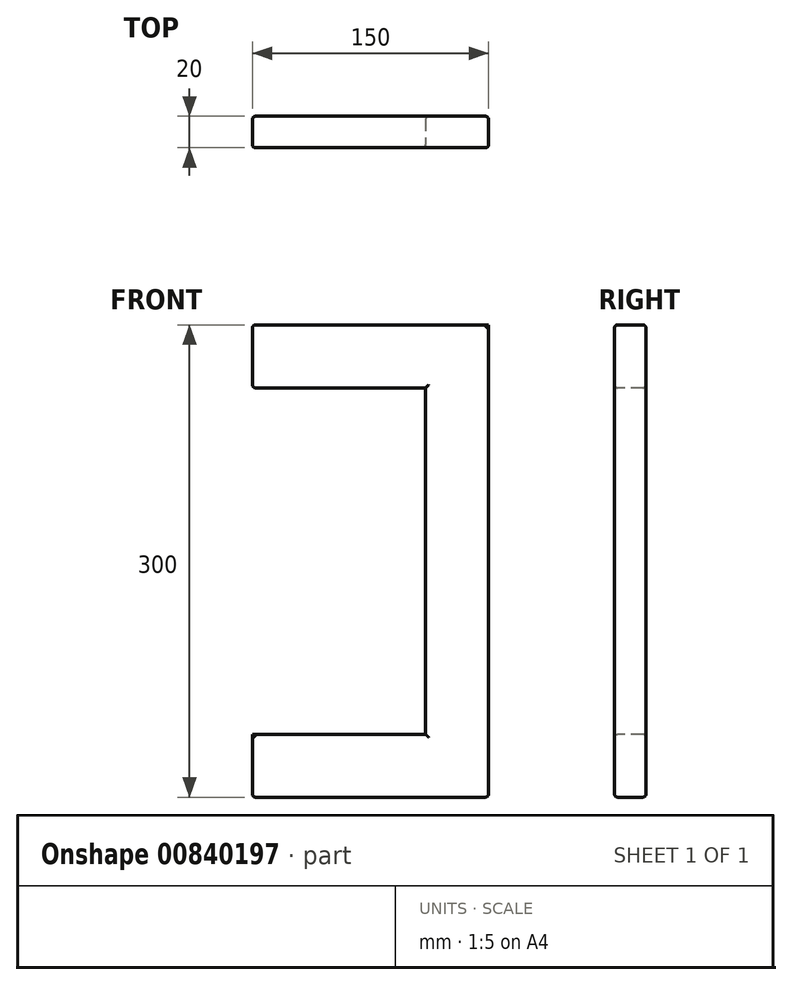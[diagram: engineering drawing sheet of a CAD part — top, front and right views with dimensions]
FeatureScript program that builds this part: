
annotation { "Feature Type Name" : "Feature", "Feature Type Description" : "" }
export const myFeature = defineFeature(function(context is Context, id is Id, definition is map)
    precondition{}
    {
        {
            var Q0;
            Q0=qCreatedBy(makeId("Top.planeOp"),FACE);
            var sketch = newSketch(context, id + "F0", { "sketchPlane" : qUnion([Q0])});
            skLineSegment(sketch, "E0.bottom", {"start": v(-48.59, 39.95) * mm, "end": v(-8.59, 39.95) * mm});
            skLineSegment(sketch, "E0.top", {"start": v(-48.59, 19.95) * mm, "end": v(-8.59, 19.95) * mm});
            skLineSegment(sketch, "E0.left", {"start": v(-48.59, 39.95) * mm, "end": v(-48.59, 19.95) * mm});
            skLineSegment(sketch, "E0.right", {"start": v(-8.59, 39.95) * mm, "end": v(-8.59, 19.95) * mm});
            skSolve(sketch);
        }
        {
            var Q0;
            Q0=makeQuery(id+"F0.imprint","IMPRINT",FACE,{"disambiguationData":[TD([[makeQuery(id+"F0.imprint","IMPRINT",EDGE,{"derivedFrom":sQuery(id+"F0.wireOp",EDGE,"E0.bottom")}),-1.0]])]});
            extrude(context, id + "F1", {"entities" : qUnion([Q0]), "depth" : 300 * mm, "offsetDistance" : 25 * mm});
        }
        {
            var Q0;
            Q0=makeQuery(id+"F1.opExtrude","SWEPT_FACE",FACE,{"disambiguationData":[OSD([sQuery(id+"F0.wireOp",EDGE,"E0.bottom")])]});
            var sketch = newSketch(context, id + "F2", { "sketchPlane" : qUnion([Q0])});
            skLineSegment(sketch, "E1", {"start": v(8.59, 300) * mm, "end": v(158.59, 300) * mm});
            skLineSegment(sketch, "E2", {"start": v(158.59, 300) * mm, "end": v(158.59, 260) * mm});
            skLineSegment(sketch, "E3", {"start": v(158.59, 260) * mm, "end": v(8.59, 260) * mm});
            skLineSegment(sketch, "E4", {"start": v(8.59, 260) * mm, "end": v(8.59, 300) * mm});
            skLineSegment(sketch, "E5", {"start": v(8.59, 0) * mm, "end": v(158.59, 0) * mm});
            skLineSegment(sketch, "E6", {"start": v(158.59, 0) * mm, "end": v(158.59, 40) * mm});
            skLineSegment(sketch, "E7", {"start": v(158.59, 40) * mm, "end": v(8.59, 40) * mm});
            skLineSegment(sketch, "E8", {"start": v(8.59, 40) * mm, "end": v(8.59, 0) * mm});
            skSolve(sketch);
        }
        {
            var Q0;
            {var subQ3=sQuery(id+"F2.wireOp",EDGE,"E2");Q0=makeQuery(id+"F2.imprint","IMPRINT",FACE,{"disambiguationData":[TD([[makeQuery(id+"F2.imprint","IMPRINT",EDGE,{"derivedFrom":subQ3}),-1.0]])]});}
            var Q1;
            {var subQ4=sQuery(id+"F2.wireOp",EDGE,"E4");Q1=makeQuery(id+"F2.imprint","IMPRINT",FACE,{"disambiguationData":[TD([[makeQuery(id+"F2.imprint","IMPRINT",EDGE,{"derivedFrom":subQ4}),1.0]])]});}
            var Q2;
            {var subQ4=sQuery(id+"F2.wireOp",EDGE,"E8");Q2=makeQuery(id+"F2.imprint","IMPRINT",FACE,{"disambiguationData":[TD([[makeQuery(id+"F2.imprint","IMPRINT",EDGE,{"derivedFrom":subQ4}),1.0]])]});}
            var Q3;
            {var subQ3=sQuery(id+"F2.wireOp",EDGE,"E6");Q3=makeQuery(id+"F2.imprint","IMPRINT",FACE,{"disambiguationData":[TD([[makeQuery(id+"F2.imprint","IMPRINT",EDGE,{"derivedFrom":subQ3}),1.0]])]});}
            extrude(context, id + "F3", {"entities" : qUnion([Q0, Q1, Q2, Q3]), "operationType" : NewBodyOperationType.ADD, "depth" : -20 * mm, "offsetDistance" : 25 * mm});
        }
        {
            var Q0;
            Q0=makeQuery(id+"F3.opExtrude","CAP_EDGE",EDGE,{"disambiguationData":[OSD([sQuery(id+"F2.wireOp",EDGE,"E3")])],"isStart":false});
            var Q1;
            Q1=makeQuery(id+"F1.opExtrude","SWEPT_EDGE",EDGE,{"disambiguationData":[OSD([sQuery(id+"F0.wireOp",EDGE,"E0.top"),sQuery(id+"F0.wireOp",EDGE,"E0.left")])]});
            var Q2;
            Q2=makeQuery(id+"F1.opExtrude","SWEPT_EDGE",EDGE,{"disambiguationData":[OSD([sQuery(id+"F0.wireOp",EDGE,"E0.top"),sQuery(id+"F0.wireOp",EDGE,"E0.right")])]});
            var Q3;
            Q3=makeQuery(id+"F3.boolean.opBoolean","MERGE",EDGE,{"derivedFrom":[makeQuery(id+"F1.opExtrude","CAP_EDGE",EDGE,{"disambiguationData":[OSD([sQuery(id+"F0.wireOp",EDGE,"E0.top")])],"isStart":false}),makeQuery(id+"F3.opExtrude","CAP_EDGE",EDGE,{"disambiguationData":[OSD([sQuery(id+"F2.wireOp",EDGE,"E1")])],"isStart":false})]});
            var Q4;
            Q4=makeQuery(id+"F3.opExtrude","CAP_EDGE",EDGE,{"disambiguationData":[OSD([sQuery(id+"F2.wireOp",EDGE,"E2")])],"isStart":false});
            var Q5;
            Q5=makeQuery(id+"F3.opExtrude","CAP_EDGE",EDGE,{"disambiguationData":[OSD([sQuery(id+"F2.wireOp",EDGE,"E2")])],"isStart":true});
            var Q6;
            Q6=makeQuery(id+"F3.opExtrude","SWEPT_EDGE",EDGE,{"disambiguationData":[OSD([sQuery(id+"F2.wireOp",EDGE,"E2"),sQuery(id+"F2.wireOp",EDGE,"E3")])]});
            var Q7;
            Q7=makeQuery(id+"F3.opExtrude","SWEPT_EDGE",EDGE,{"disambiguationData":[OSD([sQuery(id+"F2.wireOp",EDGE,"E1"),sQuery(id+"F2.wireOp",EDGE,"E2")])]});
            var Q8;
            Q8=makeQuery(id+"F3.boolean.opBoolean","MERGE",EDGE,{"derivedFrom":[makeQuery(id+"F1.opExtrude","CAP_EDGE",EDGE,{"disambiguationData":[OSD([sQuery(id+"F0.wireOp",EDGE,"E0.bottom")])],"isStart":false}),makeQuery(id+"F3.opExtrude","CAP_EDGE",EDGE,{"disambiguationData":[OSD([sQuery(id+"F2.wireOp",EDGE,"E1")])],"isStart":true})]});
            var Q9;
            Q9=makeQuery(id+"F3.opExtrude","CAP_EDGE",EDGE,{"disambiguationData":[OSD([sQuery(id+"F2.wireOp",EDGE,"E3")])],"isStart":true});
            var Q10;
            Q10=makeQuery(id+"F1.opExtrude","SWEPT_EDGE",EDGE,{"disambiguationData":[OSD([sQuery(id+"F0.wireOp",EDGE,"E0.bottom"),sQuery(id+"F0.wireOp",EDGE,"E0.left")])]});
            var Q11;
            Q11=makeQuery(id+"F1.opExtrude","SWEPT_EDGE",EDGE,{"disambiguationData":[OSD([sQuery(id+"F0.wireOp",EDGE,"E0.bottom"),sQuery(id+"F0.wireOp",EDGE,"E0.right")])]});
            var Q12;
            Q12=makeQuery(id+"F1.opExtrude","CAP_EDGE",EDGE,{"disambiguationData":[OSD([sQuery(id+"F0.wireOp",EDGE,"E0.right")])],"isStart":true});
            var Q13;
            Q13=makeQuery(id+"F3.boolean.opBoolean","MERGE",EDGE,{"derivedFrom":[makeQuery(id+"F1.opExtrude","CAP_EDGE",EDGE,{"disambiguationData":[OSD([sQuery(id+"F0.wireOp",EDGE,"E0.bottom")])],"isStart":true}),makeQuery(id+"F3.opExtrude","CAP_EDGE",EDGE,{"disambiguationData":[OSD([sQuery(id+"F2.wireOp",EDGE,"E5")])],"isStart":true})]});
            var Q14;
            Q14=makeQuery(id+"F3.boolean.opBoolean","MERGE",EDGE,{"derivedFrom":[makeQuery(id+"F1.opExtrude","CAP_EDGE",EDGE,{"disambiguationData":[OSD([sQuery(id+"F0.wireOp",EDGE,"E0.top")])],"isStart":true}),makeQuery(id+"F3.opExtrude","CAP_EDGE",EDGE,{"disambiguationData":[OSD([sQuery(id+"F2.wireOp",EDGE,"E5")])],"isStart":false})]});
            var Q15;
            Q15=makeQuery(id+"F3.opExtrude","SWEPT_EDGE",EDGE,{"disambiguationData":[OSD([sQuery(id+"F2.wireOp",EDGE,"E5"),sQuery(id+"F2.wireOp",EDGE,"E6")])]});
            var Q16;
            Q16=makeQuery(id+"F3.opExtrude","CAP_EDGE",EDGE,{"disambiguationData":[OSD([sQuery(id+"F2.wireOp",EDGE,"E6")])],"isStart":true});
            var Q17;
            Q17=makeQuery(id+"F3.opExtrude","CAP_EDGE",EDGE,{"disambiguationData":[OSD([sQuery(id+"F2.wireOp",EDGE,"E6")])],"isStart":false});
            var Q18;
            Q18=makeQuery(id+"F3.opExtrude","CAP_EDGE",EDGE,{"disambiguationData":[OSD([sQuery(id+"F2.wireOp",EDGE,"E7")])],"isStart":false});
            var Q19;
            Q19=makeQuery(id+"F3.opExtrude","CAP_EDGE",EDGE,{"disambiguationData":[OSD([sQuery(id+"F2.wireOp",EDGE,"E7")])],"isStart":true});
            fillet(context, id + "F4", {"entities" : qUnion([Q0, Q1, Q2, Q3, Q4, Q5, Q6, Q7, Q8, Q9, Q10, Q11, Q12, Q13, Q14, Q15, Q16, Q17, Q18, Q19]), "tangentPropagation" : true, "radius" : 2 * mm, "defaultsChanged" : false, "vertexSettings" : [], "allowEdgeOverflow" : false});
        }
    });
